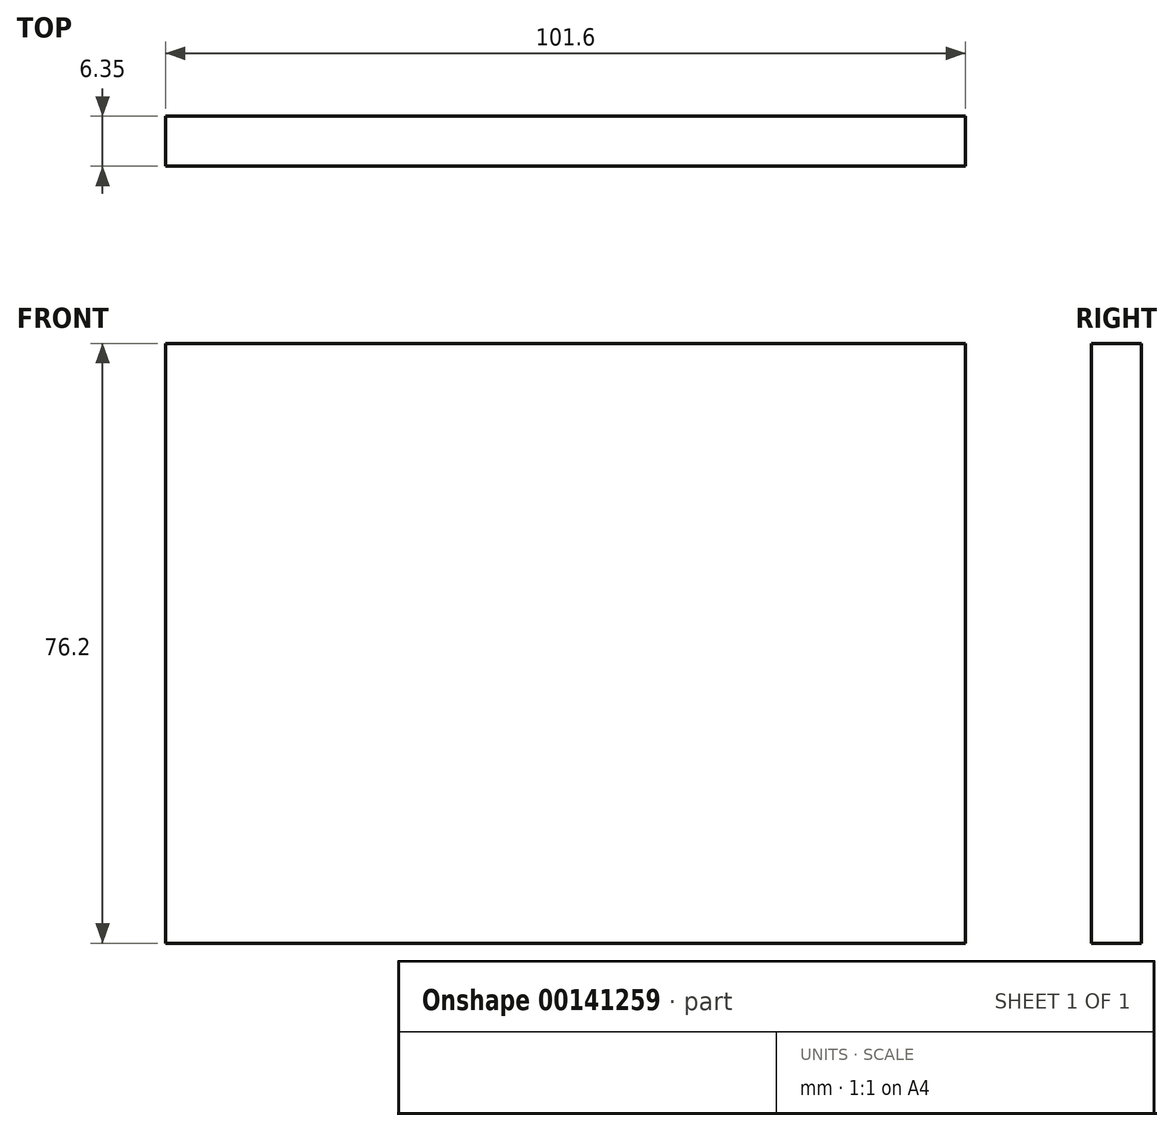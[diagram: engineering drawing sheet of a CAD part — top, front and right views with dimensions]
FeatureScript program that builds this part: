
annotation { "Feature Type Name" : "Feature", "Feature Type Description" : "" }
export const myFeature = defineFeature(function(context is Context, id is Id, definition is map)
    precondition{}
    {
        {
            var Q0;
            Q0=qCreatedBy(makeId("Front.planeOp"),FACE);
            var sketch = newSketch(context, id + "F0", { "sketchPlane" : qUnion([Q0])});
            skLineSegment(sketch, "E0.bottom", {"start": v(-50.8, 38.1) * mm, "end": v(50.8, 38.1) * mm});
            skLineSegment(sketch, "E0.top", {"start": v(-50.8, -38.1) * mm, "end": v(50.8, -38.1) * mm});
            skLineSegment(sketch, "E0.left", {"start": v(-50.8, 38.1) * mm, "end": v(-50.8, -38.1) * mm});
            skLineSegment(sketch, "E0.right", {"start": v(50.8, 38.1) * mm, "end": v(50.8, -38.1) * mm});
            skPoint(sketch, "E0.middle", {"position": v(0, 0) * mm});
            skSolve(sketch);
        }
        {
            var Q0;
            Q0 = qSketchRegion(id + "F0", true);
            extrude(context, id + "F1", {"entities" : qUnion([Q0]), "depth" : 6.35 * mm});
        }
    });
